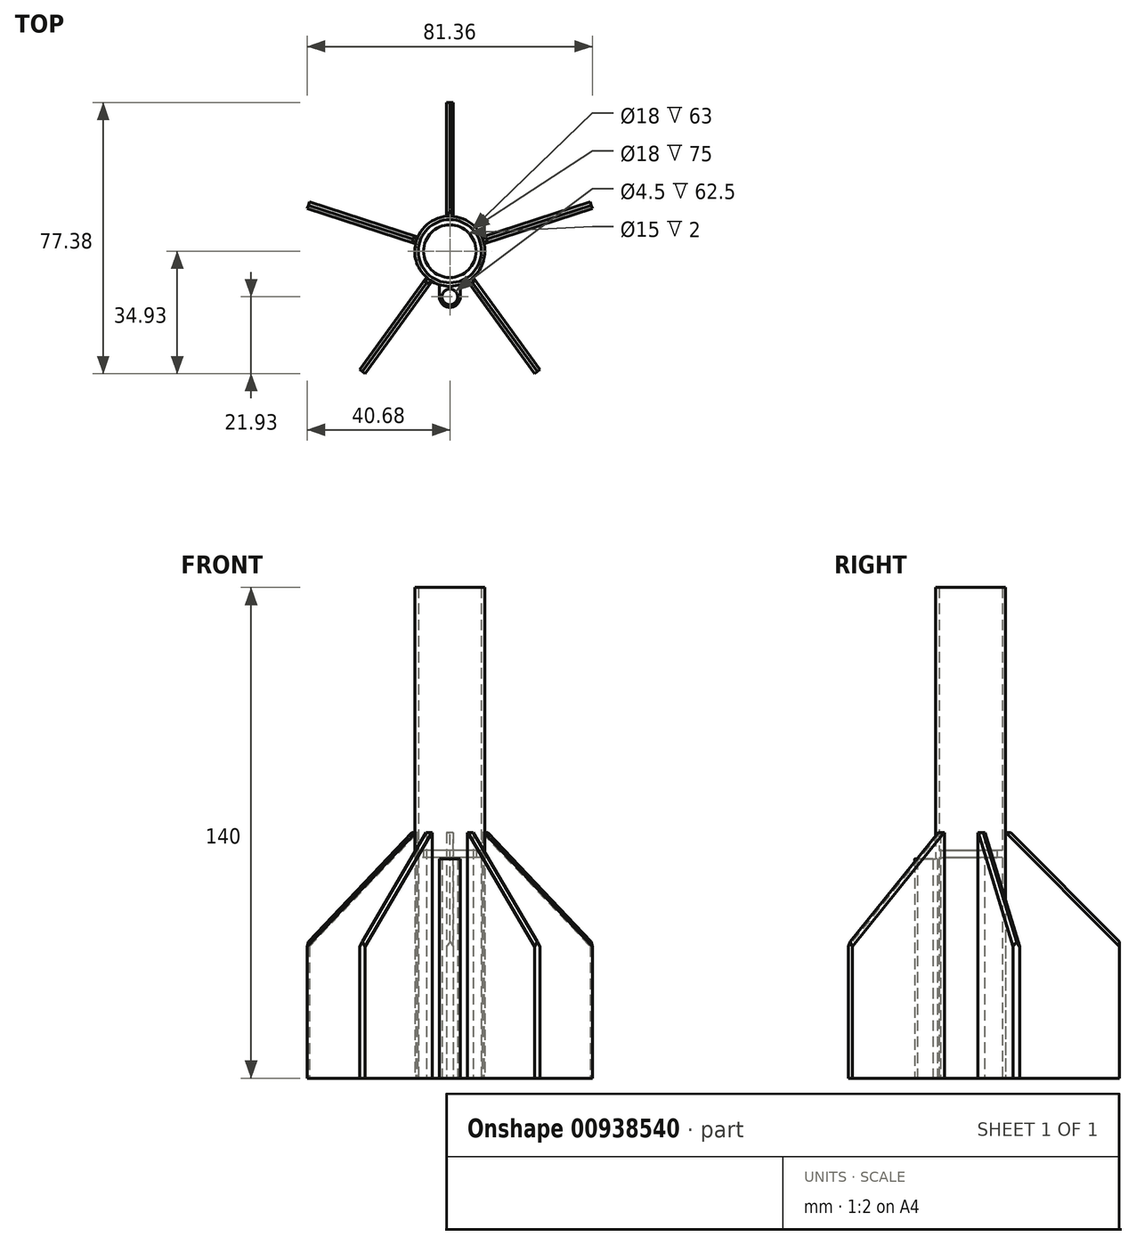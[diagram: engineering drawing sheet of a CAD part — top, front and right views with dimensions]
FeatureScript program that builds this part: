
annotation { "Feature Type Name" : "Feature", "Feature Type Description" : "" }
export const myFeature = defineFeature(function(context is Context, id is Id, definition is map)
    precondition{}
    {
        {
            var Q0;
            Q0=qCreatedBy(makeId("Top.planeOp"),FACE);
            var sketch = newSketch(context, id + "F0", { "sketchPlane" : qUnion([Q0])});
            skCircle(sketch, "E0", {"center": v(0, 0) * mm, "radius": 9 * mm});
            skCircle(sketch, "E1", {"center": v(0, 0) * mm, "radius": 10 * mm});
            skCircle(sketch, "E2", {"center": v(0, -13) * mm, "radius": 2.25 * mm});
            skCircle(sketch, "E3", {"center": v(0, -13) * mm, "radius": 3 * mm});
            skLineSegment(sketch, "E4", {"start": v(-3, -13) * mm, "end": v(-3, -9.54) * mm});
            skLineSegment(sketch, "E5", {"start": v(3, -13) * mm, "end": v(3, -9.54) * mm});
            skLineSegment(sketch, "E6.bottom", {"start": v(-1, 42.45) * mm, "end": v(1, 42.45) * mm});
            skLineSegment(sketch, "E6.top", {"start": v(-1, 9.95) * mm, "end": v(1, 9.95) * mm, "construction": true});
            skLineSegment(sketch, "E6.left", {"start": v(-1, 42.45) * mm, "end": v(-1, 9.95) * mm});
            skLineSegment(sketch, "E6.right", {"start": v(1, 42.45) * mm, "end": v(1, 9.95) * mm});
            skCircle(sketch, "E7", {"center": v(0, 0) * mm, "radius": 7.5 * mm});
            skSolve(sketch);
        }
        {
            var Q0;
            Q0=makeQuery(id+"F0.imprint","IMPRINT",FACE,{"disambiguationData":[TD([[makeQuery(id+"F0.imprint","IMPRINT",EDGE,{"derivedFrom":sQuery(id+"F0.wireOp",EDGE,"E0")}),-1.0]])]});
            extrude(context, id + "F1", {"entities" : qUnion([Q0]), "depth" : 140 * mm, "offsetDistance" : 25 * mm});
        }
        {
            var Q0;
            Q0=makeQuery(id+"F0.imprint","IMPRINT",FACE,{"disambiguationData":[TD([[makeQuery(id+"F0.imprint","IMPRINT",EDGE,{"derivedFrom":sQuery(id+"F0.wireOp",EDGE,"E6.bottom")}),-1.0]])]});
            extrude(context, id + "F2", {"entities" : qUnion([Q0]), "operationType" : NewBodyOperationType.ADD, "depth" : 70 * mm, "offsetDistance" : 25 * mm});
        }
        {
            var Q0;
            Q0=makeQuery(id+"F2.opExtrude","CAP_EDGE",EDGE,{"disambiguationData":[OSD([sQuery(id+"F0.wireOp",EDGE,"E6.bottom")])],"isStart":false});
            chamfer(context, id + "F3", {"entities" : qUnion([Q0]), "width" : 31 * mm, "tangentPropagation" : true});
        }
        {
            var Q0;
            Q0=makeQuery(id+"F3.opChamfer","BLEND_EDGE",EDGE,{"blendedFrom":[makeQuery(id+"F2.opExtrude","CAP_EDGE",EDGE,{"disambiguationData":[OSD([sQuery(id+"F0.wireOp",EDGE,"E6.bottom")])],"isStart":false}),makeQuery(id+"F2.opExtrude","SWEPT_FACE",FACE,{"disambiguationData":[OSD([sQuery(id+"F0.wireOp",EDGE,"E6.left")])]})],"blendedInto":[makeQuery(id+"F2.opExtrude","SWEPT_FACE",FACE,{"disambiguationData":[OSD([sQuery(id+"F0.wireOp",EDGE,"E6.left")])]})]});
            var Q1;
            Q1=makeQuery(id+"F3.opChamfer","BLEND_EDGE",EDGE,{"blendedFrom":[makeQuery(id+"F2.opExtrude","CAP_EDGE",EDGE,{"disambiguationData":[OSD([sQuery(id+"F0.wireOp",EDGE,"E6.bottom")])],"isStart":false}),makeQuery(id+"F2.opExtrude","SWEPT_FACE",FACE,{"disambiguationData":[OSD([sQuery(id+"F0.wireOp",EDGE,"E6.right")])]})],"blendedInto":[makeQuery(id+"F2.opExtrude","SWEPT_FACE",FACE,{"disambiguationData":[OSD([sQuery(id+"F0.wireOp",EDGE,"E6.right")])]})]});
            chamfer(context, id + "F4", {"entities" : qUnion([Q0, Q1]), "width" : 1 * mm, "tangentPropagation" : true});
        }
        {
            var Q0;
            Q0=makeQuery(id+"F1.opExtrude","SWEPT_BODY",BODY,{"disambiguationData":[OSD([sQuery(id+"F0.wireOp",EDGE,"E0"),sQuery(id+"F0.wireOp",EDGE,"E1")])]});
            var Q1;
            Q1=makeQuery(id+"F1.opExtrude","SWEPT_FACE",FACE,{"disambiguationData":[OSD([sQuery(id+"F0.wireOp",EDGE,"E0")])]});
            circularPattern(context, id + "F5", {"operationType" : NewBodyOperationType.ADD, "entities" : qUnion([Q0]), "axis" : qUnion([Q1]), "angle" : 360 * degree, "instanceCount" : 5, "equalSpace" : true});
        }
        {
            var Q0;
            {var subQ0=sQuery(id+"F0.wireOp",EDGE,"E4");Q0=makeQuery(id+"F0.imprint","IMPRINT",FACE,{"disambiguationData":[TD([[makeQuery(id+"F0.imprint","IMPRINT",EDGE,{"derivedFrom":subQ0}),-1.0]])]});}
            var Q1;
            {var subQ0=sQuery(id+"F0.wireOp",EDGE,"E5");Q1=makeQuery(id+"F0.imprint","IMPRINT",FACE,{"disambiguationData":[TD([[makeQuery(id+"F0.imprint","IMPRINT",EDGE,{"derivedFrom":subQ0}),1.0]])]});}
            var Q2;
            Q2=makeQuery(id+"F0.imprint","IMPRINT",FACE,{"disambiguationData":[TD([[makeQuery(id+"F0.imprint","IMPRINT",EDGE,{"derivedFrom":sQuery(id+"F0.wireOp",EDGE,"E2")}),-1.0]])]});
            extrude(context, id + "F6", {"entities" : qUnion([Q0, Q1, Q2]), "operationType" : NewBodyOperationType.ADD, "depth" : 62.5 * mm, "offsetDistance" : 25 * mm});
        }
        {
            var Q0;
            Q0=makeQuery(id+"F0.imprint","IMPRINT",FACE,{"disambiguationData":[TD([[makeQuery(id+"F0.imprint","IMPRINT",EDGE,{"derivedFrom":sQuery(id+"F0.wireOp",EDGE,"E0")}),1.0]])]});
            extrude(context, id + "F7", {"entities" : qUnion([Q0]), "operationType" : NewBodyOperationType.ADD, "depth" : 65 * mm, "offsetDistance" : 25 * mm, "hasSecondDirection" : true, "secondDirectionOppositeDirection" : false, "secondDirectionDepth" : 63 * mm});
        }
    });
